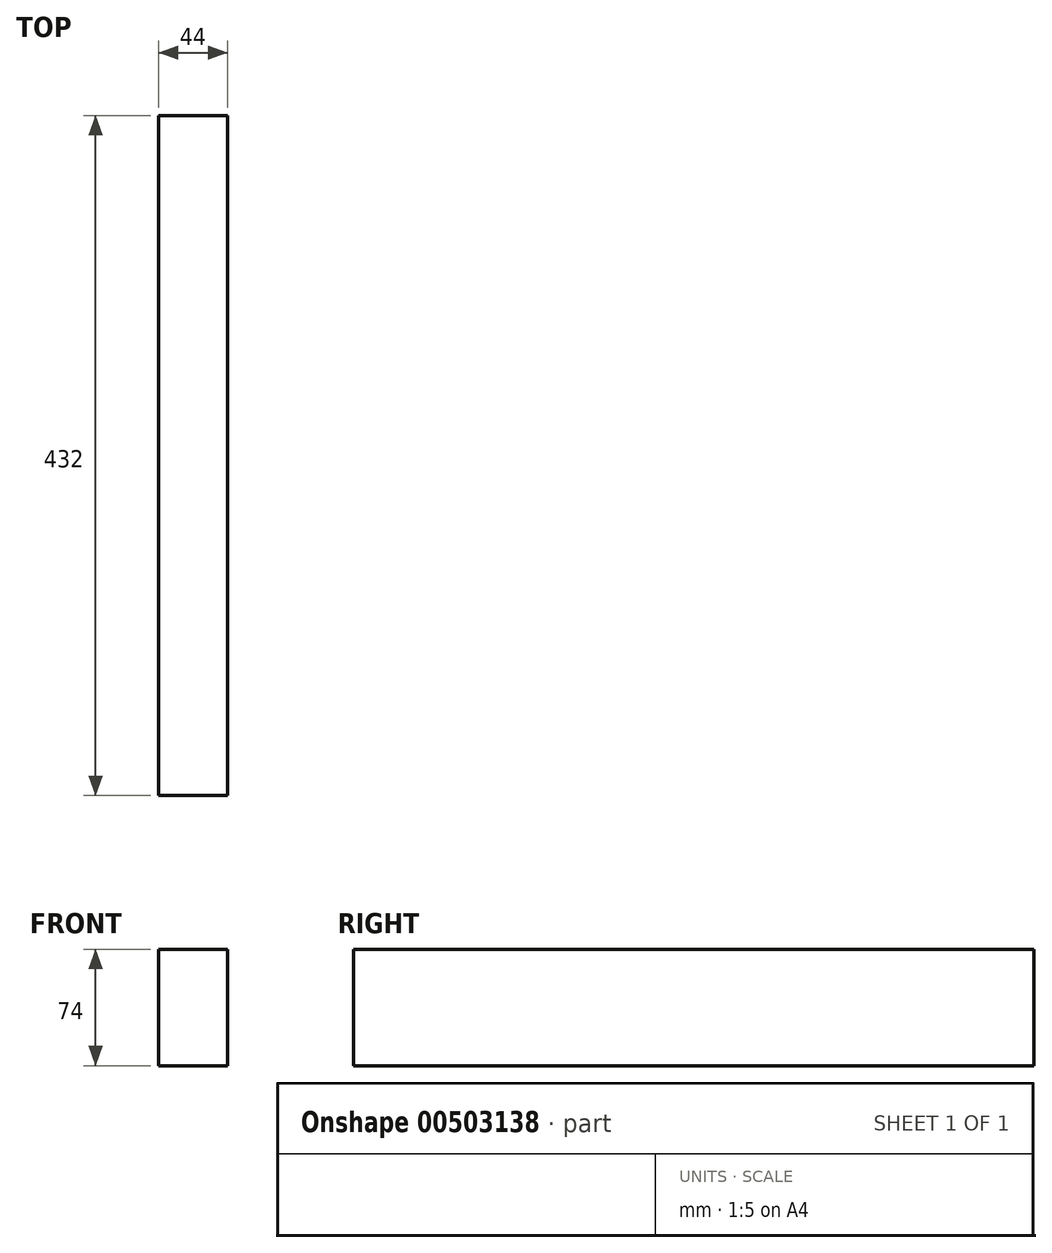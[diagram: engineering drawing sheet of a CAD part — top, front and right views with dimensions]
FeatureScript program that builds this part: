
annotation { "Feature Type Name" : "Feature", "Feature Type Description" : "" }
export const myFeature = defineFeature(function(context is Context, id is Id, definition is map)
    precondition{}
    {
        {
            var Q0;
            Q0=qCreatedBy(makeId("Right.planeOp"),FACE);
            var sketch = newSketch(context, id + "F0", { "sketchPlane" : qUnion([Q0])});
            skLineSegment(sketch, "E0.bottom", {"start": v(300, 45) * mm, "end": v(-132, 45) * mm});
            skLineSegment(sketch, "E0.top", {"start": v(300, -29) * mm, "end": v(-132, -29) * mm});
            skLineSegment(sketch, "E0.left", {"start": v(300, 45) * mm, "end": v(300, -29) * mm});
            skLineSegment(sketch, "E0.right", {"start": v(-132, 45) * mm, "end": v(-132, -29) * mm});
            skSolve(sketch);
        }
        {
            var Q0;
            Q0=makeQuery(id+"F0.imprint","IMPRINT",FACE,{"disambiguationData":[TD([[makeQuery(id+"F0.imprint","IMPRINT",EDGE,{"derivedFrom":sQuery(id+"F0.wireOp",EDGE,"E0.bottom")}),1.0]])]});
            extrude(context, id + "F1", {"entities" : qUnion([Q0]), "depth" : 44 * mm, "offsetDistance" : 25 * mm});
        }
    });
